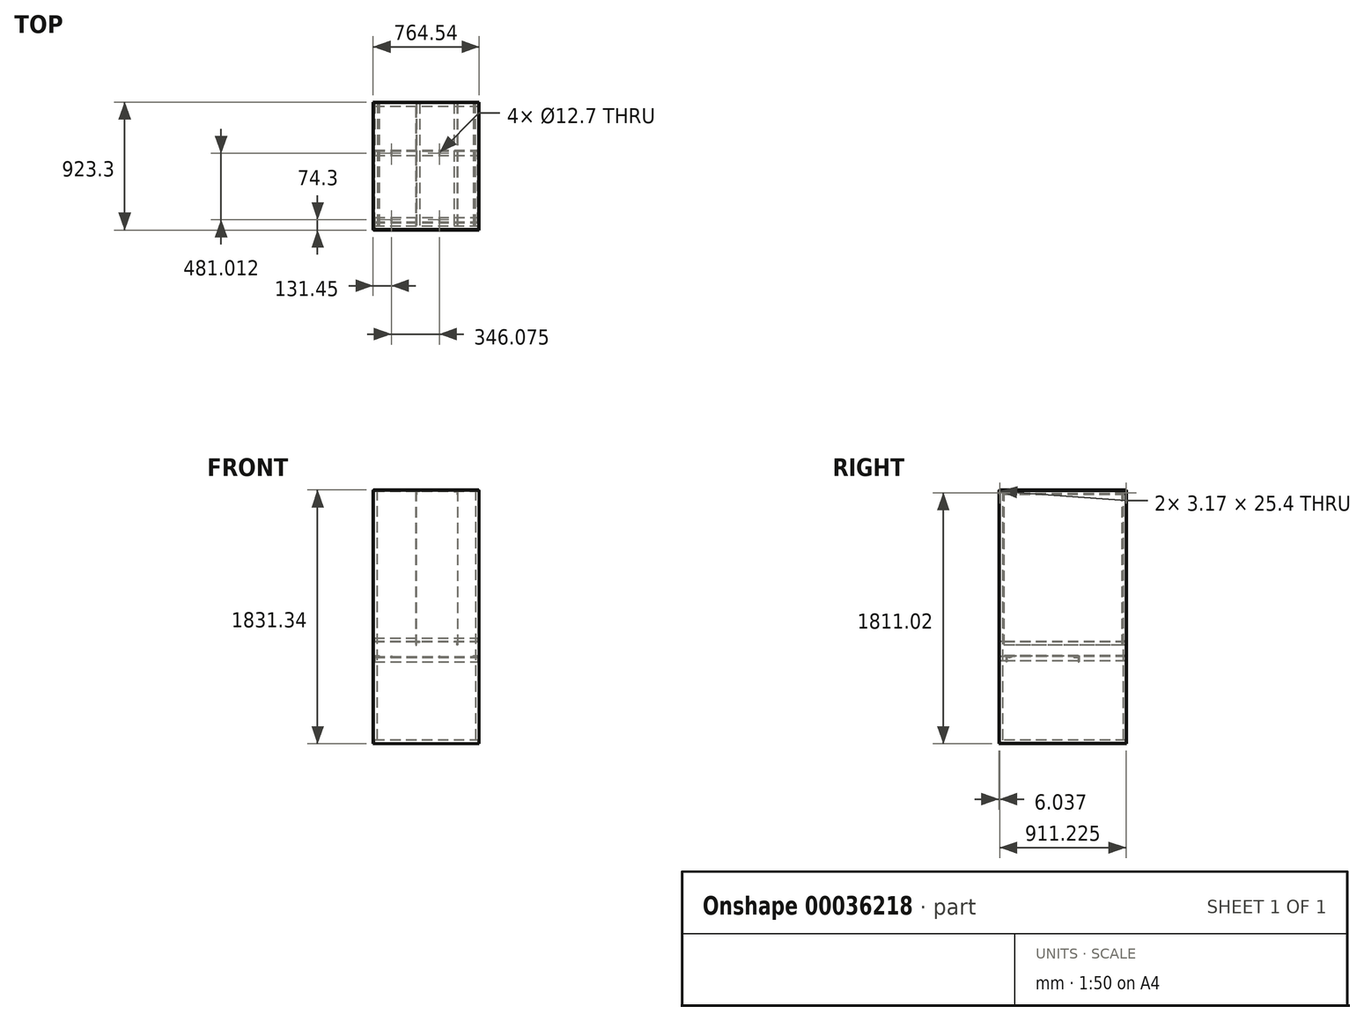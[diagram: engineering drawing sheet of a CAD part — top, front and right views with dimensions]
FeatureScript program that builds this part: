
annotation { "Feature Type Name" : "Feature", "Feature Type Description" : "" }
export const myFeature = defineFeature(function(context is Context, id is Id, definition is map)
    precondition{}
    {
        {
            var Q0;
            Q0=qCreatedBy(makeId("Front.planeOp"),FACE);
            var sketch = newSketch(context, id + "F0", { "sketchPlane" : qUnion([Q0])});
            skLineSegment(sketch, "E0", {"start": v(0, 0) * mm, "end": v(0, 25.4) * mm});
            skLineSegment(sketch, "E1", {"start": v(0, 25.4) * mm, "end": v(3.18, 25.4) * mm});
            skLineSegment(sketch, "E2", {"start": v(3.18, 25.4) * mm, "end": v(3.18, 3.17) * mm});
            skLineSegment(sketch, "E3", {"start": v(3.18, 3.17) * mm, "end": v(25.4, 3.17) * mm});
            skLineSegment(sketch, "E4", {"start": v(25.4, 3.17) * mm, "end": v(25.4, 0) * mm});
            skLineSegment(sketch, "E5", {"start": v(25.4, 0) * mm, "end": v(0, 0) * mm});
            skLineSegment(sketch, "E6", {"start": v(730.25, 0) * mm, "end": v(755.65, 0) * mm});
            skLineSegment(sketch, "E7", {"start": v(755.65, 0) * mm, "end": v(755.65, 25.4) * mm});
            skLineSegment(sketch, "E8", {"start": v(755.65, 25.4) * mm, "end": v(752.48, 25.4) * mm});
            skLineSegment(sketch, "E9", {"start": v(752.47, 25.4) * mm, "end": v(752.47, 3.18) * mm});
            skLineSegment(sketch, "E10", {"start": v(752.47, 3.18) * mm, "end": v(730.25, 3.18) * mm});
            skLineSegment(sketch, "E11", {"start": v(730.25, 3.18) * mm, "end": v(730.25, 0) * mm});
            skLineSegment(sketch, "E12", {"start": v(730.25, 1828.8) * mm, "end": v(755.65, 1828.8) * mm});
            skLineSegment(sketch, "E13", {"start": v(755.65, 1828.8) * mm, "end": v(755.65, 1803.4) * mm});
            skLineSegment(sketch, "E14", {"start": v(755.65, 1803.4) * mm, "end": v(752.48, 1803.4) * mm});
            skLineSegment(sketch, "E15", {"start": v(752.48, 1803.4) * mm, "end": v(752.48, 1825.62) * mm});
            skLineSegment(sketch, "E16", {"start": v(752.47, 1825.62) * mm, "end": v(730.25, 1825.62) * mm});
            skLineSegment(sketch, "E17", {"start": v(730.25, 1825.62) * mm, "end": v(730.25, 1828.8) * mm});
            skLineSegment(sketch, "E18", {"start": v(0, 1803.4) * mm, "end": v(0, 1828.8) * mm});
            skLineSegment(sketch, "E19", {"start": v(0, 1828.8) * mm, "end": v(25.4, 1828.8) * mm});
            skLineSegment(sketch, "E20", {"start": v(25.4, 1828.8) * mm, "end": v(25.4, 1825.62) * mm});
            skLineSegment(sketch, "E21", {"start": v(25.4, 1825.62) * mm, "end": v(3.17, 1825.62) * mm});
            skLineSegment(sketch, "E22", {"start": v(3.17, 1825.62) * mm, "end": v(3.17, 1803.4) * mm});
            skLineSegment(sketch, "E23", {"start": v(3.17, 1803.4) * mm, "end": v(0, 1803.4) * mm});
            skLineSegment(sketch, "E24", {"start": v(717.55, 635) * mm, "end": v(755.65, 635) * mm});
            skLineSegment(sketch, "E25", {"start": v(755.65, 635) * mm, "end": v(755.65, 596.9) * mm});
            skLineSegment(sketch, "E26", {"start": v(755.65, 596.9) * mm, "end": v(749.3, 596.9) * mm});
            skLineSegment(sketch, "E27", {"start": v(749.3, 596.9) * mm, "end": v(749.3, 628.65) * mm});
            skLineSegment(sketch, "E28", {"start": v(749.3, 628.65) * mm, "end": v(717.55, 628.65) * mm});
            skLineSegment(sketch, "E29", {"start": v(717.55, 628.65) * mm, "end": v(717.55, 635) * mm});
            skLineSegment(sketch, "E30", {"start": v(0, 596.9) * mm, "end": v(0, 635) * mm});
            skLineSegment(sketch, "E31", {"start": v(0, 635) * mm, "end": v(38.1, 635) * mm});
            skLineSegment(sketch, "E32", {"start": v(38.1, 635) * mm, "end": v(38.1, 628.65) * mm});
            skLineSegment(sketch, "E33", {"start": v(38.1, 628.65) * mm, "end": v(6.35, 628.65) * mm});
            skLineSegment(sketch, "E34", {"start": v(6.35, 628.65) * mm, "end": v(6.35, 596.9) * mm});
            skLineSegment(sketch, "E35", {"start": v(6.35, 596.9) * mm, "end": v(0, 596.9) * mm});
            skLineSegment(sketch, "E36", {"start": v(577.85, 736.6) * mm, "end": v(603.25, 736.6) * mm});
            skLineSegment(sketch, "E37", {"start": v(603.25, 736.6) * mm, "end": v(603.25, 711.2) * mm});
            skLineSegment(sketch, "E38", {"start": v(603.25, 711.2) * mm, "end": v(600.07, 711.2) * mm});
            skLineSegment(sketch, "E39", {"start": v(600.07, 711.2) * mm, "end": v(600.07, 733.43) * mm});
            skLineSegment(sketch, "E40", {"start": v(600.07, 733.43) * mm, "end": v(577.85, 733.43) * mm});
            skLineSegment(sketch, "E41", {"start": v(577.85, 1822.45) * mm, "end": v(603.25, 1822.45) * mm});
            skLineSegment(sketch, "E42", {"start": v(603.25, 1822.45) * mm, "end": v(603.25, 1797.05) * mm});
            skLineSegment(sketch, "E43", {"start": v(603.25, 1797.05) * mm, "end": v(600.07, 1797.05) * mm});
            skLineSegment(sketch, "E44", {"start": v(600.07, 1797.05) * mm, "end": v(600.07, 1819.27) * mm});
            skLineSegment(sketch, "E45", {"start": v(600.07, 1819.27) * mm, "end": v(577.85, 1819.27) * mm});
            skLineSegment(sketch, "E46", {"start": v(577.85, 1819.27) * mm, "end": v(577.85, 1822.45) * mm});
            skLineSegment(sketch, "E47", {"start": v(577.85, 736.6) * mm, "end": v(577.85, 733.43) * mm});
            skLineSegment(sketch, "E48", {"start": v(600.07, 733.43) * mm, "end": v(600.07, 736.6) * mm, "construction": true});
            skLineSegment(sketch, "E49", {"start": v(600.07, 1819.27) * mm, "end": v(600.07, 1822.45) * mm, "construction": true});
            skLineSegment(sketch, "E50.MirrorCS", {"start": v(307.97, 733.43) * mm, "end": v(307.97, 736.6) * mm, "construction": true});
            skLineSegment(sketch, "E51.MirrorCS", {"start": v(330.2, 736.6) * mm, "end": v(330.2, 733.43) * mm});
            skLineSegment(sketch, "E52.MirrorCS", {"start": v(330.2, 736.6) * mm, "end": v(304.8, 736.6) * mm});
            skLineSegment(sketch, "E53.MirrorCS", {"start": v(307.97, 733.43) * mm, "end": v(330.2, 733.43) * mm});
            skLineSegment(sketch, "E54.MirrorCS", {"start": v(304.8, 736.6) * mm, "end": v(304.8, 711.2) * mm});
            skLineSegment(sketch, "E55.MirrorCS", {"start": v(307.97, 711.2) * mm, "end": v(307.97, 733.43) * mm});
            skLineSegment(sketch, "E56.MirrorCS", {"start": v(304.8, 711.2) * mm, "end": v(307.97, 711.2) * mm});
            skLineSegment(sketch, "E57.MirrorCS", {"start": v(307.97, 1819.27) * mm, "end": v(307.97, 1822.45) * mm, "construction": true});
            skLineSegment(sketch, "E58.MirrorCS", {"start": v(330.2, 1822.45) * mm, "end": v(304.8, 1822.45) * mm});
            skLineSegment(sketch, "E59.MirrorCS", {"start": v(307.97, 1819.27) * mm, "end": v(330.2, 1819.27) * mm});
            skLineSegment(sketch, "E60.MirrorCS", {"start": v(304.8, 1822.45) * mm, "end": v(304.8, 1797.05) * mm});
            skLineSegment(sketch, "E61.MirrorCS", {"start": v(307.97, 1797.05) * mm, "end": v(307.97, 1819.27) * mm});
            skLineSegment(sketch, "E62.MirrorCS", {"start": v(330.2, 1819.27) * mm, "end": v(330.2, 1822.45) * mm});
            skLineSegment(sketch, "E63.MirrorCS", {"start": v(304.8, 1797.05) * mm, "end": v(307.97, 1797.05) * mm});
            skSolve(sketch);
        }
        {
            var Q0;
            Q0=qSketchRegion(id+"F0",true);
            extrude(context, id + "F1", {"entities" : qUnion([Q0]), "oppositeDirection" : true, "depth" : 914.4 * mm});
        }
        {
            var Q0;
            Q0=qCreatedBy(makeId("Top.planeOp"),FACE);
            var sketch = newSketch(context, id + "F2", { "sketchPlane" : qUnion([Q0])});
            skLineSegment(sketch, "E64", {"start": v(-3.18, 22.23) * mm, "end": v(-3.18, -3.18) * mm});
            skLineSegment(sketch, "E65", {"start": v(-3.18, -3.18) * mm, "end": v(22.23, -3.18) * mm});
            skLineSegment(sketch, "E66", {"start": v(22.23, -3.18) * mm, "end": v(22.23, 0) * mm});
            skLineSegment(sketch, "E67", {"start": v(22.23, 0) * mm, "end": v(0, 0) * mm});
            skLineSegment(sketch, "E68", {"start": v(0, 0) * mm, "end": v(0, 22.23) * mm});
            skLineSegment(sketch, "E69", {"start": v(0, 22.23) * mm, "end": v(-3.18, 22.23) * mm});
            skLineSegment(sketch, "E70", {"start": v(733.42, -3.18) * mm, "end": v(758.83, -3.18) * mm});
            skLineSegment(sketch, "E71", {"start": v(758.83, -3.18) * mm, "end": v(758.83, 22.23) * mm});
            skLineSegment(sketch, "E72", {"start": v(758.83, 22.23) * mm, "end": v(755.65, 22.23) * mm});
            skLineSegment(sketch, "E73", {"start": v(755.65, 22.23) * mm, "end": v(755.65, 0) * mm});
            skLineSegment(sketch, "E74", {"start": v(755.65, 0) * mm, "end": v(733.42, 0) * mm});
            skLineSegment(sketch, "E75", {"start": v(733.42, 0) * mm, "end": v(733.42, -3.18) * mm});
            skLineSegment(sketch, "E76", {"start": v(0, 892.17) * mm, "end": v(0, 914.4) * mm});
            skLineSegment(sketch, "E77", {"start": v(0, 914.4) * mm, "end": v(22.23, 914.4) * mm});
            skLineSegment(sketch, "E78", {"start": v(22.23, 914.4) * mm, "end": v(22.23, 917.58) * mm});
            skLineSegment(sketch, "E79", {"start": v(22.23, 917.58) * mm, "end": v(-3.18, 917.58) * mm});
            skLineSegment(sketch, "E80", {"start": v(-3.18, 917.58) * mm, "end": v(-3.18, 892.17) * mm});
            skLineSegment(sketch, "E81", {"start": v(-3.18, 892.17) * mm, "end": v(0, 892.17) * mm});
            skLineSegment(sketch, "E82", {"start": v(733.42, 914.4) * mm, "end": v(755.65, 914.4) * mm});
            skLineSegment(sketch, "E83", {"start": v(755.65, 914.4) * mm, "end": v(755.65, 892.17) * mm});
            skLineSegment(sketch, "E84", {"start": v(755.65, 892.18) * mm, "end": v(758.83, 892.18) * mm});
            skLineSegment(sketch, "E85", {"start": v(758.83, 892.17) * mm, "end": v(758.83, 917.58) * mm});
            skLineSegment(sketch, "E86", {"start": v(758.83, 917.58) * mm, "end": v(733.42, 917.58) * mm});
            skLineSegment(sketch, "E87", {"start": v(733.42, 917.58) * mm, "end": v(733.42, 914.4) * mm});
            skSolve(sketch);
        }
        {
            var Q0;
            Q0=qSketchRegion(id+"F2",true);
            extrude(context, id + "F3", {"entities" : qUnion([Q0]), "depth" : 1828.8 * mm});
        }
        {
            var Q0;
            Q0=makeQuery(id+"F1.opExtrude","SWEPT_FACE",FACE,{"disambiguationData":[OSD([sQuery(id+"F0.wireOp",EDGE,"E15")])]});
            var sketch = newSketch(context, id + "F4", { "sketchPlane" : qUnion([Q0])});
            skLineSegment(sketch, "E88", {"start": v(-25.4, 3.18) * mm, "end": v(0, 3.18) * mm});
            skLineSegment(sketch, "E89", {"start": v(0, 3.18) * mm, "end": v(0, 28.58) * mm});
            skLineSegment(sketch, "E90", {"start": v(0, 28.58) * mm, "end": v(-3.17, 28.58) * mm});
            skLineSegment(sketch, "E91", {"start": v(-3.18, 28.58) * mm, "end": v(-3.17, 6.35) * mm});
            skLineSegment(sketch, "E92", {"start": v(-3.18, 6.35) * mm, "end": v(-25.4, 6.35) * mm});
            skLineSegment(sketch, "E93", {"start": v(-25.4, 6.35) * mm, "end": v(-25.4, 3.18) * mm});
            skLineSegment(sketch, "E94", {"start": v(0, 1800.22) * mm, "end": v(0, 1825.62) * mm});
            skLineSegment(sketch, "E95", {"start": v(0, 1825.62) * mm, "end": v(-25.4, 1825.62) * mm});
            skLineSegment(sketch, "E96", {"start": v(-25.4, 1825.62) * mm, "end": v(-25.4, 1822.45) * mm});
            skLineSegment(sketch, "E97", {"start": v(-25.4, 1822.45) * mm, "end": v(-3.18, 1822.45) * mm});
            skLineSegment(sketch, "E98", {"start": v(-3.18, 1822.45) * mm, "end": v(-3.18, 1800.22) * mm});
            skLineSegment(sketch, "E99", {"start": v(-3.18, 1800.22) * mm, "end": v(0, 1800.22) * mm});
            skLineSegment(sketch, "E100", {"start": v(-914.4, 1800.22) * mm, "end": v(-914.4, 1825.62) * mm});
            skLineSegment(sketch, "E101", {"start": v(-914.4, 1825.62) * mm, "end": v(-889, 1825.62) * mm});
            skLineSegment(sketch, "E102", {"start": v(-889, 1825.62) * mm, "end": v(-889, 1822.45) * mm});
            skLineSegment(sketch, "E103", {"start": v(-889, 1822.45) * mm, "end": v(-911.22, 1822.45) * mm});
            skLineSegment(sketch, "E104", {"start": v(-911.23, 1822.45) * mm, "end": v(-911.23, 1800.22) * mm});
            skLineSegment(sketch, "E105", {"start": v(-911.22, 1800.22) * mm, "end": v(-914.4, 1800.22) * mm});
            skLineSegment(sketch, "E106", {"start": v(-914.4, 28.58) * mm, "end": v(-914.4, 3.18) * mm});
            skLineSegment(sketch, "E107", {"start": v(-914.4, 3.18) * mm, "end": v(-889, 3.18) * mm});
            skLineSegment(sketch, "E108", {"start": v(-889, 3.18) * mm, "end": v(-889, 6.35) * mm});
            skLineSegment(sketch, "E109", {"start": v(-889, 6.35) * mm, "end": v(-911.22, 6.35) * mm});
            skLineSegment(sketch, "E110", {"start": v(-911.22, 6.35) * mm, "end": v(-911.22, 28.58) * mm});
            skLineSegment(sketch, "E111", {"start": v(-911.22, 28.58) * mm, "end": v(-914.4, 28.58) * mm});
            skLineSegment(sketch, "E112", {"start": v(-573.09, 590.55) * mm, "end": v(-573.09, 628.65) * mm});
            skLineSegment(sketch, "E113", {"start": v(-573.09, 628.65) * mm, "end": v(-534.99, 628.65) * mm});
            skLineSegment(sketch, "E114", {"start": v(-534.99, 628.65) * mm, "end": v(-534.99, 622.3) * mm});
            skLineSegment(sketch, "E115", {"start": v(-534.99, 622.3) * mm, "end": v(-566.74, 622.3) * mm});
            skLineSegment(sketch, "E116", {"start": v(-566.74, 622.3) * mm, "end": v(-566.74, 590.55) * mm});
            skLineSegment(sketch, "E117", {"start": v(-566.74, 590.55) * mm, "end": v(-573.09, 590.55) * mm});
            skLineSegment(sketch, "E118", {"start": v(-550.86, 622.3) * mm, "end": v(-550.86, 628.65) * mm, "construction": true});
            skLineSegment(sketch, "E119", {"start": v(-47.63, 590.55) * mm, "end": v(-47.63, 628.65) * mm});
            skLineSegment(sketch, "E120", {"start": v(-47.63, 628.65) * mm, "end": v(-85.72, 628.65) * mm});
            skLineSegment(sketch, "E121", {"start": v(-85.73, 628.65) * mm, "end": v(-85.73, 622.3) * mm});
            skLineSegment(sketch, "E122", {"start": v(-85.72, 622.3) * mm, "end": v(-53.98, 622.3) * mm});
            skLineSegment(sketch, "E123", {"start": v(-53.98, 622.3) * mm, "end": v(-53.98, 590.55) * mm});
            skLineSegment(sketch, "E124", {"start": v(-53.97, 590.55) * mm, "end": v(-47.63, 590.55) * mm});
            skLineSegment(sketch, "E125", {"start": v(-69.85, 622.3) * mm, "end": v(-69.85, 628.65) * mm, "construction": true});
            skLineSegment(sketch, "E126", {"start": v(-550.86, 625.48) * mm, "end": v(-69.85, 625.48) * mm, "construction": true});
            skLineSegment(sketch, "E127", {"start": v(0, 736.6) * mm, "end": v(0, 762) * mm});
            skLineSegment(sketch, "E128", {"start": v(0, 762) * mm, "end": v(-3.17, 762) * mm});
            skLineSegment(sketch, "E129", {"start": v(-3.17, 762) * mm, "end": v(-3.17, 739.78) * mm});
            skLineSegment(sketch, "E130", {"start": v(-3.17, 739.78) * mm, "end": v(-25.4, 739.78) * mm});
            skLineSegment(sketch, "E131", {"start": v(-25.4, 739.78) * mm, "end": v(-25.4, 736.6) * mm});
            skLineSegment(sketch, "E132", {"start": v(-25.4, 736.6) * mm, "end": v(0, 736.6) * mm});
            skLineSegment(sketch, "E133", {"start": v(-889, 736.6) * mm, "end": v(-914.4, 736.6) * mm});
            skLineSegment(sketch, "E134", {"start": v(-914.4, 736.6) * mm, "end": v(-914.4, 762) * mm});
            skLineSegment(sketch, "E135", {"start": v(-914.4, 762) * mm, "end": v(-911.22, 762) * mm});
            skLineSegment(sketch, "E136", {"start": v(-911.23, 762) * mm, "end": v(-911.23, 739.78) * mm});
            skLineSegment(sketch, "E137", {"start": v(-911.22, 739.78) * mm, "end": v(-889, 739.78) * mm});
            skLineSegment(sketch, "E138", {"start": v(-889, 739.78) * mm, "end": v(-889, 736.6) * mm});
            skSolve(sketch);
        }
        {
            var Q0;
            Q0=qSketchRegion(id+"F4",true);
            var Q1;
            Q1=makeQuery(id+"F1.opExtrude","SWEPT_FACE",FACE,{"disambiguationData":[OSD([sQuery(id+"F0.wireOp",EDGE,"E2")])]});
            extrude(context, id + "F5", {"entities" : qUnion([Q0]), "endBound" : BoundingType.UP_TO_SURFACE, "endBoundEntityFace" : qUnion([Q1]), "depth" : 25.4 * mm});
        }
        {
            var Q0;
            Q0=makeQuery(id+"F5.opExtrude","SWEPT_FACE",FACE,{"disambiguationData":[OSD([sQuery(id+"F4.wireOp",EDGE,"E115")])]});
            var sketch = newSketch(context, id + "F6", { "sketchPlane" : qUnion([Q0])});
            skLineSegment(sketch, "E139.bottom", {"start": v(127, -69.85) * mm, "end": v(473.07, -69.85) * mm, "construction": true});
            skLineSegment(sketch, "E139.top", {"start": v(127, -550.86) * mm, "end": v(473.07, -550.86) * mm, "construction": true});
            skLineSegment(sketch, "E139.left", {"start": v(473.07, -69.85) * mm, "end": v(473.07, -550.86) * mm, "construction": true});
            skLineSegment(sketch, "E139.right", {"start": v(127, -69.85) * mm, "end": v(127, -550.86) * mm, "construction": true});
            skLineSegment(sketch, "E140", {"start": v(473.07, -550.86) * mm, "end": v(3.17, -550.86) * mm, "construction": true});
            skLineSegment(sketch, "E141", {"start": v(127, -550.86) * mm, "end": v(752.47, -550.86) * mm, "construction": true});
            skCircle(sketch, "E142", {"center": v(127, -69.85) * mm, "radius": 6.35 * mm});
            skCircle(sketch, "E143", {"center": v(473.07, -69.85) * mm, "radius": 6.35 * mm});
            skCircle(sketch, "E144", {"center": v(473.07, -550.86) * mm, "radius": 6.35 * mm});
            skCircle(sketch, "E145", {"center": v(127, -550.86) * mm, "radius": 6.35 * mm});
            skLineSegment(sketch, "E146.bottom", {"start": v(3.17, -47.62) * mm, "end": v(6.35, -47.62) * mm});
            skLineSegment(sketch, "E146.top", {"start": v(3.17, -573.09) * mm, "end": v(6.35, -573.09) * mm});
            skLineSegment(sketch, "E146.left", {"start": v(3.17, -47.62) * mm, "end": v(3.17, -573.09) * mm});
            skLineSegment(sketch, "E146.right", {"start": v(6.35, -47.62) * mm, "end": v(6.35, -573.09) * mm});
            skLineSegment(sketch, "E147.bottom", {"start": v(749.3, -47.62) * mm, "end": v(752.47, -47.62) * mm});
            skLineSegment(sketch, "E147.top", {"start": v(749.3, -573.09) * mm, "end": v(752.47, -573.09) * mm});
            skLineSegment(sketch, "E147.left", {"start": v(749.3, -47.62) * mm, "end": v(749.3, -573.09) * mm});
            skLineSegment(sketch, "E147.right", {"start": v(752.47, -47.62) * mm, "end": v(752.47, -573.09) * mm});
            skSolve(sketch);
        }
        {
            var Q0;
            Q0=makeQuery(id+"F6.imprint","IMPRINT",FACE,{"disambiguationData":[TD([[makeQuery(id+"F6.imprint","IMPRINT",EDGE,{"derivedFrom":sQuery(id+"F6.wireOp",EDGE,"E143")}),1.0]])]});
            var Q1;
            Q1=makeQuery(id+"F6.imprint","IMPRINT",FACE,{"disambiguationData":[TD([[makeQuery(id+"F6.imprint","IMPRINT",EDGE,{"derivedFrom":sQuery(id+"F6.wireOp",EDGE,"E144")}),1.0]])]});
            var Q2;
            Q2=makeQuery(id+"F6.imprint","IMPRINT",FACE,{"disambiguationData":[TD([[makeQuery(id+"F6.imprint","IMPRINT",EDGE,{"derivedFrom":sQuery(id+"F6.wireOp",EDGE,"E145")}),1.0]])]});
            var Q3;
            Q3=makeQuery(id+"F6.imprint","IMPRINT",FACE,{"disambiguationData":[TD([[makeQuery(id+"F6.imprint","IMPRINT",EDGE,{"derivedFrom":sQuery(id+"F6.wireOp",EDGE,"E142")}),1.0]])]});
            var Q4;
            {var subQ5=sQuery(id+"F6.wireOp",EDGE,"E146.bottom");Q4=makeQuery(id+"F6.imprint","IMPRINT",FACE,{"disambiguationData":[TD([[makeQuery(id+"F6.imprint","IMPRINT",EDGE,{"derivedFrom":subQ5}),-1.0]])]});}
            var Q5;
            {var subQ5=sQuery(id+"F6.wireOp",EDGE,"E147.bottom");Q5=makeQuery(id+"F6.imprint","IMPRINT",FACE,{"disambiguationData":[TD([[makeQuery(id+"F6.imprint","IMPRINT",EDGE,{"derivedFrom":subQ5}),-1.0]])]});}
            var Q6;
            {var subQ5=sQuery(id+"F6.wireOp",EDGE,"E146.top");Q6=makeQuery(id+"F6.imprint","IMPRINT",FACE,{"disambiguationData":[TD([[makeQuery(id+"F6.imprint","IMPRINT",EDGE,{"derivedFrom":subQ5}),1.0]])]});}
            var Q7;
            {var subQ0=sQuery(id+"F4.wireOp",EDGE,"E115");var subQ4=sQuery(id+"F6.wireOp",EDGE,"E146.left");var subQ6=makeQuery(id+"F5.opExtrude","SWEPT_EDGE",EDGE,{"disambiguationData":[OSD([sQuery(id+"F4.wireOp",EDGE,"E114"),subQ0])]});var subQ8=makeQuery(id+"F6.imprint","INTERSECT",VERTEX,{"derivedFrom":[subQ6,subQ4]});Q7=makeQuery(id+"F6.imprint","IMPRINT",FACE,{"disambiguationData":[TD([[makeQuery(id+"F6.imprint","IMPRINT",EDGE,{"disambiguationData":[TD([[subQ8,-1.0]])],"derivedFrom":subQ4}),1.0]])]});}
            var Q8;
            {var subQ0=sQuery(id+"F4.wireOp",EDGE,"E115");var subQ2=sQuery(id+"F6.wireOp",EDGE,"E147.left");var subQ6=makeQuery(id+"F5.opExtrude","SWEPT_EDGE",EDGE,{"disambiguationData":[OSD([sQuery(id+"F4.wireOp",EDGE,"E114"),subQ0])]});var subQ7=makeQuery(id+"F6.imprint","INTERSECT",VERTEX,{"derivedFrom":[subQ6,subQ2]});Q8=makeQuery(id+"F6.imprint","IMPRINT",FACE,{"disambiguationData":[TD([[makeQuery(id+"F6.imprint","IMPRINT",EDGE,{"disambiguationData":[TD([[subQ7,-1.0]])],"derivedFrom":subQ2}),1.0]])]});}
            var Q9;
            {var subQ5=sQuery(id+"F6.wireOp",EDGE,"E147.top");Q9=makeQuery(id+"F6.imprint","IMPRINT",FACE,{"disambiguationData":[TD([[makeQuery(id+"F6.imprint","IMPRINT",EDGE,{"derivedFrom":subQ5}),1.0]])]});}
            var Q10;
            Q10=makeQuery(id+"F5.opExtrude","SWEPT_FACE",FACE,{"disambiguationData":[OSD([sQuery(id+"F4.wireOp",EDGE,"E117")])]});
            extrude(context, id + "F7", {"entities" : qUnion([Q0, Q1, Q2, Q3, Q4, Q5, Q6, Q7, Q8, Q9]), "operationType" : NewBodyOperationType.REMOVE, "oppositeDirection" : true, "endBoundEntityFace" : qUnion([Q10]), "depth" : 50.8 * mm, "hasSecondDirection" : true, "secondDirectionOppositeDirection" : false, "secondDirectionDepth" : 50.8 * mm});
        }
        {
            var Q0;
            Q0=makeQuery(id+"F1.opExtrude","SWEPT_FACE",FACE,{"disambiguationData":[OSD([sQuery(id+"F0.wireOp",EDGE,"E37")])]});
            var sketch = newSketch(context, id + "F8", { "sketchPlane" : qUnion([Q0])});
            skLineSegment(sketch, "E148.bottom", {"start": v(31.75, 1822.45) * mm, "end": v(882.65, 1822.45) * mm});
            skLineSegment(sketch, "E148.top", {"start": v(31.75, 711.2) * mm, "end": v(882.65, 711.2) * mm});
            skLineSegment(sketch, "E148.left", {"start": v(31.75, 1822.45) * mm, "end": v(31.75, 711.2) * mm});
            skLineSegment(sketch, "E148.right", {"start": v(882.65, 1822.45) * mm, "end": v(882.65, 711.2) * mm});
            skSolve(sketch);
        }
        {
            var Q0;
            Q0=qSketchRegion(id+"F8",true);
            extrude(context, id + "F9", {"entities" : qUnion([Q0]), "depth" : 1.27 * mm});
        }
        {
            var Q0;
            Q0=makeQuery(id+"F1.opExtrude","SWEPT_FACE",FACE,{"disambiguationData":[OSD([sQuery(id+"F0.wireOp",EDGE,"E46")])]});
            var sketch = newSketch(context, id + "F10", { "sketchPlane" : qUnion([Q0])});
            skLineSegment(sketch, "E149.bottom", {"start": v(-3.18, 1822.45) * mm, "end": v(0, 1822.45) * mm});
            skLineSegment(sketch, "E149.top", {"start": v(-3.18, 1797.05) * mm, "end": v(0, 1797.05) * mm});
            skLineSegment(sketch, "E149.left", {"start": v(-3.18, 1822.45) * mm, "end": v(-3.18, 1797.05) * mm});
            skLineSegment(sketch, "E149.right", {"start": v(0, 1822.45) * mm, "end": v(0, 1797.05) * mm});
            skLineSegment(sketch, "E150.bottom", {"start": v(-914.4, 1822.45) * mm, "end": v(-911.22, 1822.45) * mm});
            skLineSegment(sketch, "E150.top", {"start": v(-914.4, 1797.05) * mm, "end": v(-911.22, 1797.05) * mm});
            skLineSegment(sketch, "E150.left", {"start": v(-914.4, 1822.45) * mm, "end": v(-914.4, 1797.05) * mm});
            skLineSegment(sketch, "E150.right", {"start": v(-911.22, 1822.45) * mm, "end": v(-911.22, 1797.05) * mm});
            skSolve(sketch);
        }
        {
            var Q0;
            Q0 = qSketchRegion(id + "F10", true);
            var Q1;
            Q1=makeQuery(id+"F1.opExtrude","SWEPT_FACE",FACE,{"disambiguationData":[OSD([sQuery(id+"F0.wireOp",EDGE,"E60.MirrorCS")])]});
            extrude(context, id + "F11", {"entities" : qUnion([Q0]), "operationType" : NewBodyOperationType.REMOVE, "endBound" : BoundingType.THROUGH_ALL, "depth" : 25.4 * mm, "hasSecondDirection" : true, "secondDirectionBound" : BoundingType.THROUGH_ALL, "secondDirectionOppositeDirection" : true, "secondDirectionBoundEntityFace" : qUnion([Q1]), "secondDirectionDepth" : 508 * mm});
        }
        {
            var Q0;
            Q0=makeQuery(id+"F3.opExtrude","SWEPT_FACE",FACE,{"disambiguationData":[OSD([sQuery(id+"F2.wireOp",EDGE,"E71")])]});
            var sketch = newSketch(context, id + "F12", { "sketchPlane" : qUnion([Q0])});
            skLineSegment(sketch, "E151.bottom", {"start": v(0, 1826.02) * mm, "end": v(914.4, 1826.02) * mm});
            skLineSegment(sketch, "E151.top", {"start": v(0, 2.78) * mm, "end": v(914.4, 2.78) * mm});
            skLineSegment(sketch, "E151.left", {"start": v(0, 1826.02) * mm, "end": v(0, 2.78) * mm});
            skLineSegment(sketch, "E151.right", {"start": v(914.4, 1826.02) * mm, "end": v(914.4, 2.78) * mm});
            skLineSegment(sketch, "E152", {"start": v(914.4, 2.78) * mm, "end": v(917.58, 0) * mm, "construction": true});
            skLineSegment(sketch, "E153", {"start": v(-3.18, 0) * mm, "end": v(0, 2.78) * mm, "construction": true});
            skLineSegment(sketch, "E154", {"start": v(-3.17, 1828.8) * mm, "end": v(0, 1826.02) * mm, "construction": true});
            skLineSegment(sketch, "E155", {"start": v(914.4, 1826.02) * mm, "end": v(917.58, 1828.8) * mm, "construction": true});
            skSolve(sketch);
        }
        {
            var Q0;
            Q0=makeQuery(id+"F1.opExtrude","SWEPT_FACE",FACE,{"disambiguationData":[OSD([sQuery(id+"F0.wireOp",EDGE,"E60.MirrorCS")])]});
            var sketch = newSketch(context, id + "F13", { "sketchPlane" : qUnion([Q0])});
            skLineSegment(sketch, "E156.bottom", {"start": v(-882.65, 1822.45) * mm, "end": v(-31.75, 1822.45) * mm});
            skLineSegment(sketch, "E156.top", {"start": v(-882.65, 711.2) * mm, "end": v(-31.75, 711.2) * mm});
            skLineSegment(sketch, "E156.left", {"start": v(-882.65, 1822.45) * mm, "end": v(-882.65, 711.2) * mm});
            skLineSegment(sketch, "E156.right", {"start": v(-31.75, 1822.45) * mm, "end": v(-31.75, 711.2) * mm});
            skSolve(sketch);
        }
        {
            var Q0;
            Q0 = qSketchRegion(id + "F13", true);
            extrude(context, id + "F14", {"entities" : qUnion([Q0]), "depth" : 1.27 * mm});
        }
        {
            var Q0;
            Q0=makeQuery(id+"F3.opExtrude","SWEPT_FACE",FACE,{"disambiguationData":[OSD([sQuery(id+"F2.wireOp",EDGE,"E80")])]});
            var sketch = newSketch(context, id + "F15", { "sketchPlane" : qUnion([Q0])});
            skLineSegment(sketch, "E157.bottom", {"start": v(-917.58, 1828.8) * mm, "end": v(3.17, 1828.8) * mm});
            skLineSegment(sketch, "E157.top", {"start": v(-917.58, 0) * mm, "end": v(3.18, 0) * mm});
            skLineSegment(sketch, "E157.left", {"start": v(-917.58, 1828.8) * mm, "end": v(-917.58, 0) * mm});
            skLineSegment(sketch, "E157.right", {"start": v(3.17, 1828.8) * mm, "end": v(3.18, 0) * mm});
            skSolve(sketch);
        }
        {
            var Q0;
            Q0 = qSketchRegion(id + "F12", true);
            extrude(context, id + "F16", {"entities" : qUnion([Q0]), "depth" : 1.27 * mm});
        }
        {
            var Q0;
            Q0 = qSketchRegion(id + "F15", true);
            extrude(context, id + "F17", {"entities" : qUnion([Q0]), "depth" : 1.27 * mm});
        }
        {
            var Q0;
            Q0=makeQuery(id+"F1.opExtrude","SWEPT_FACE",FACE,{"disambiguationData":[OSD([sQuery(id+"F0.wireOp",EDGE,"E19")])]});
            var sketch = newSketch(context, id + "F18", { "sketchPlane" : qUnion([Q0])});
            skLineSegment(sketch, "E158.bottom", {"start": v(755.65, 914.4) * mm, "end": v(-3.18, 914.4) * mm});
            skLineSegment(sketch, "E158.top", {"start": v(755.65, 0) * mm, "end": v(-3.18, 0) * mm});
            skLineSegment(sketch, "E158.left", {"start": v(755.65, 914.4) * mm, "end": v(755.65, 0) * mm});
            skLineSegment(sketch, "E158.right", {"start": v(-3.18, 914.4) * mm, "end": v(-3.17, 0) * mm});
            skSolve(sketch);
        }
        {
            var Q0;
            Q0 = qSketchRegion(id + "F18", true);
            extrude(context, id + "F19", {"entities" : qUnion([Q0]), "depth" : 1.27 * mm});
        }
        {
            var Q0;
            Q0=makeQuery(id+"F1.opExtrude","SWEPT_FACE",FACE,{"disambiguationData":[OSD([sQuery(id+"F0.wireOp",EDGE,"E6")])]});
            var sketch = newSketch(context, id + "F20", { "sketchPlane" : qUnion([Q0])});
            skLineSegment(sketch, "E159.bottom", {"start": v(755.65, 0) * mm, "end": v(0, 0) * mm});
            skLineSegment(sketch, "E159.top", {"start": v(755.65, -914.4) * mm, "end": v(0, -914.4) * mm});
            skLineSegment(sketch, "E159.left", {"start": v(755.65, 0) * mm, "end": v(755.65, -914.4) * mm});
            skLineSegment(sketch, "E159.right", {"start": v(0, 0) * mm, "end": v(0, -914.4) * mm});
            skSolve(sketch);
        }
        {
            var Q0;
            Q0 = qSketchRegion(id + "F20", true);
            extrude(context, id + "F21", {"entities" : qUnion([Q0]), "depth" : 1.27 * mm});
        }
        {
            var Q0;
            Q0=makeQuery(id+"F3.opExtrude","SWEPT_FACE",FACE,{"disambiguationData":[OSD([sQuery(id+"F2.wireOp",EDGE,"E86")])]});
            var sketch = newSketch(context, id + "F22", { "sketchPlane" : qUnion([Q0])});
            skLineSegment(sketch, "E160.bottom", {"start": v(-755.65, 1828.8) * mm, "end": v(0, 1828.8) * mm});
            skLineSegment(sketch, "E160.top", {"start": v(-755.65, 0) * mm, "end": v(0, 0) * mm});
            skLineSegment(sketch, "E160.left", {"start": v(-755.65, 1828.8) * mm, "end": v(-755.65, 0) * mm});
            skLineSegment(sketch, "E160.right", {"start": v(0, 1828.8) * mm, "end": v(0, 0) * mm});
            skSolve(sketch);
        }
        {
            var Q0;
            Q0 = qSketchRegion(id + "F22", true);
            extrude(context, id + "F23", {"entities" : qUnion([Q0]), "depth" : 1.27 * mm});
        }
        {
            var Q0;
            Q0=makeQuery(id+"F3.opExtrude","SWEPT_FACE",FACE,{"disambiguationData":[OSD([sQuery(id+"F2.wireOp",EDGE,"E65")])]});
            var sketch = newSketch(context, id + "F24", { "sketchPlane" : qUnion([Q0])});
            skLineSegment(sketch, "E161.bottom", {"start": v(-3.18, 1828.8) * mm, "end": v(758.83, 1828.8) * mm});
            skLineSegment(sketch, "E161.top", {"start": v(-3.18, 0) * mm, "end": v(758.83, 0) * mm});
            skLineSegment(sketch, "E161.left", {"start": v(-3.18, 1828.8) * mm, "end": v(-3.18, 0) * mm});
            skLineSegment(sketch, "E161.right", {"start": v(758.83, 1828.8) * mm, "end": v(758.83, 0) * mm});
            skSolve(sketch);
        }
        {
            var Q0;
            Q0 = qSketchRegion(id + "F24", true);
            extrude(context, id + "F25", {"entities" : qUnion([Q0]), "depth" : 1.27 * mm});
        }
    });
